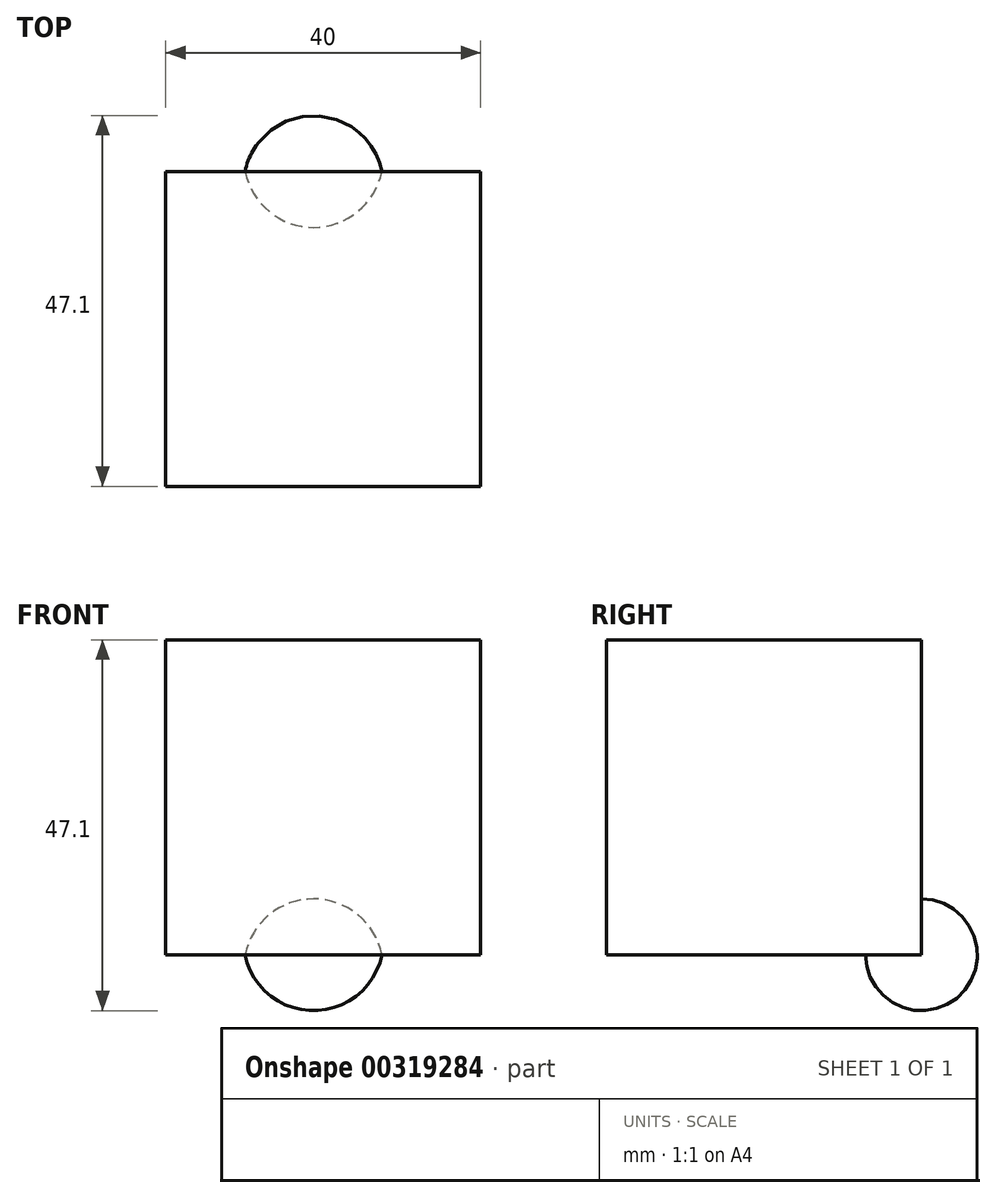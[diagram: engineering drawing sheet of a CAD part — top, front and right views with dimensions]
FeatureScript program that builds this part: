
annotation { "Feature Type Name" : "Feature", "Feature Type Description" : "" }
export const myFeature = defineFeature(function(context is Context, id is Id, definition is map)
    precondition{}
    {
        {
            var Q0;
            Q0=qCreatedBy(makeId("Front.planeOp"),FACE);
            var sketch = newSketch(context, id + "F0", { "sketchPlane" : qUnion([Q0])});
            skLineSegment(sketch, "E0.bottom", {"start": v(0, 0) * mm, "end": v(-40, 0) * mm});
            skLineSegment(sketch, "E0.top", {"start": v(0, 40) * mm, "end": v(-40, 40) * mm});
            skLineSegment(sketch, "E0.left", {"start": v(0, 0) * mm, "end": v(0, 40) * mm});
            skLineSegment(sketch, "E0.right", {"start": v(-40, 0) * mm, "end": v(-40, 40) * mm});
            skSolve(sketch);
        }
        {
            var Q0;
            Q0 = qSketchRegion(id + "F0", true);
            extrude(context, id + "F1", {"entities" : qUnion([Q0]), "depth" : 40 * mm});
        }
        {
            var Q0;
            Q0=makeQuery(id+"F1.opExtrude","CAP_FACE",FACE,{"disambiguationData":[OSD([sQuery(id+"F0.wireOp",EDGE,"E0.bottom"),sQuery(id+"F0.wireOp",EDGE,"E0.top"),sQuery(id+"F0.wireOp",EDGE,"E0.left"),sQuery(id+"F0.wireOp",EDGE,"E0.right")])],"isStart":true});
            var sketch = newSketch(context, id + "F2", { "sketchPlane" : qUnion([Q0])});
            skLineSegment(sketch, "E1", {"start": v(29.91, 0) * mm, "end": v(12.53, 0) * mm});
            skArc(sketch, "E2", {"start": v(12.53, 0) * mm, "mid": v(21.22, -7.1) * mm, "end": v(29.91, 0) * mm});
            skSolve(sketch);
        }
        {
            var Q0;
            Q0=makeQuery(id+"F2.imprint","IMPRINT",FACE,{"disambiguationData":[TD([[makeQuery(id+"F2.imprint","IMPRINT",EDGE,{"derivedFrom":sQuery(id+"F2.wireOp",EDGE,"E1")}),-1.0]])]});
            var Q1;
            Q1=sQuery(id+"F2.wireOp",EDGE,"E1");
            revolve(context, id + "F3", {"operationType" : NewBodyOperationType.ADD, "entities" : qUnion([Q0]), "axis" : qUnion([Q1]), "revolveType" : RevolveType.FULL});
        }
    });
